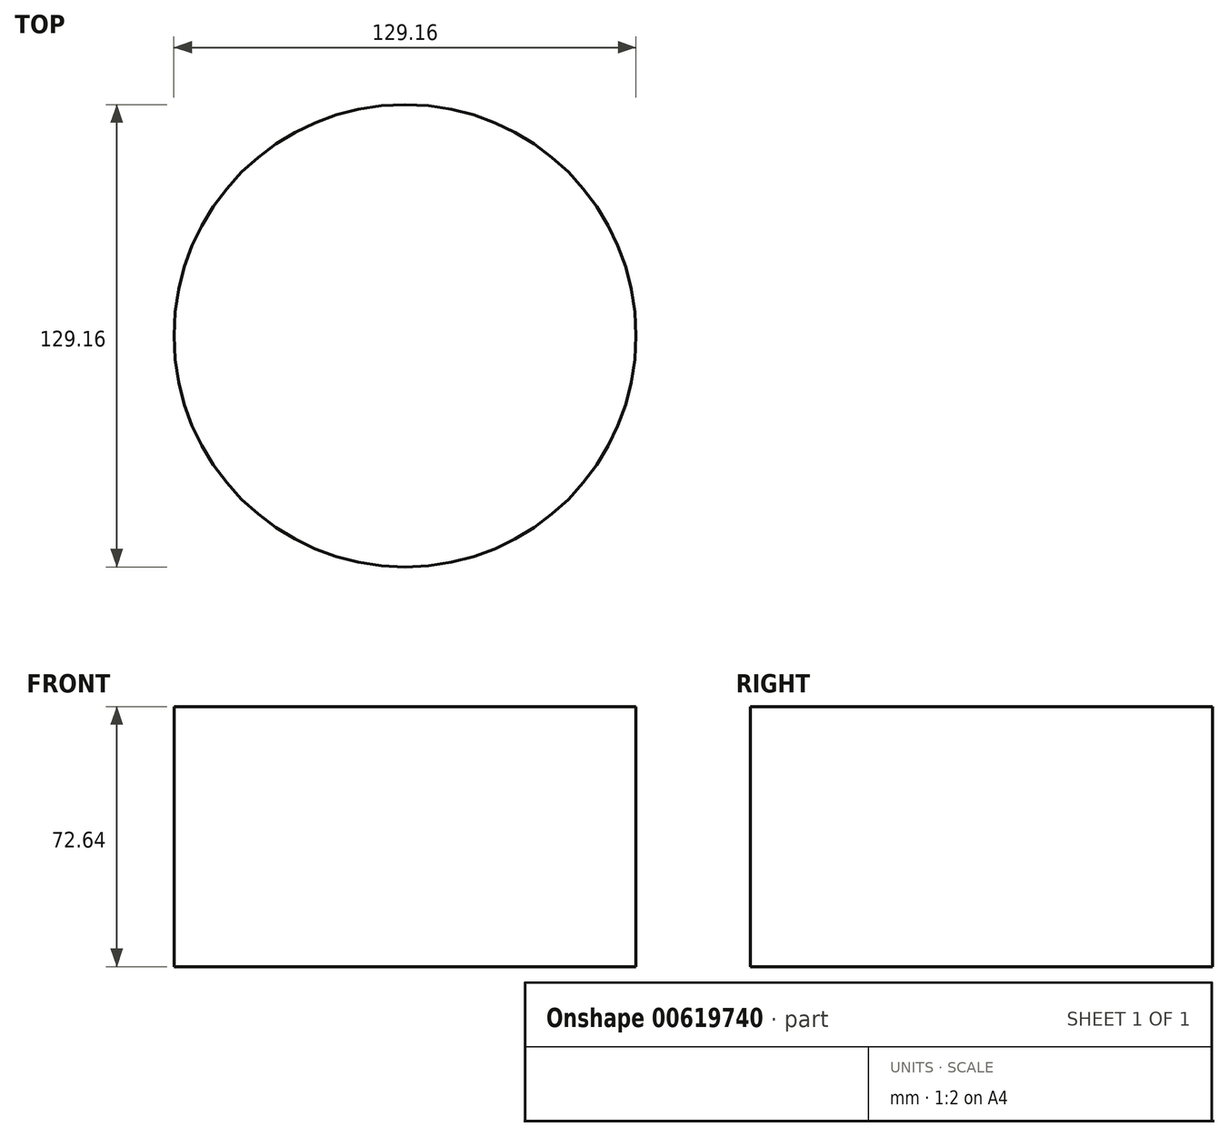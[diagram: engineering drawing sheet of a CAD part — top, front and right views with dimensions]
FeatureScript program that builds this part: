
annotation { "Feature Type Name" : "Feature", "Feature Type Description" : "" }
export const myFeature = defineFeature(function(context is Context, id is Id, definition is map)
    precondition{}
    {
        {
            var Q0;
            Q0=qCreatedBy(makeId("Top.planeOp"),FACE);
            var sketch = newSketch(context, id + "F0", { "sketchPlane" : qUnion([Q0])});
            skCircle(sketch, "E0", {"center": v(0, 0) * mm, "radius": 64.58 * mm});
            skSolve(sketch);
        }
        {
            var Q0;
            Q0=makeQuery(id+"F0.imprint","IMPRINT",FACE,{"disambiguationData":[TD([[makeQuery(id+"F0.imprint","IMPRINT",EDGE,{"derivedFrom":sQuery(id+"F0.wireOp",EDGE,"E0")}),1.0]])]});
            extrude(context, id + "F1", {"entities" : qUnion([Q0]), "depth" : 72.64 * mm, "offsetDistance" : 25.4 * mm});
        }
    });
